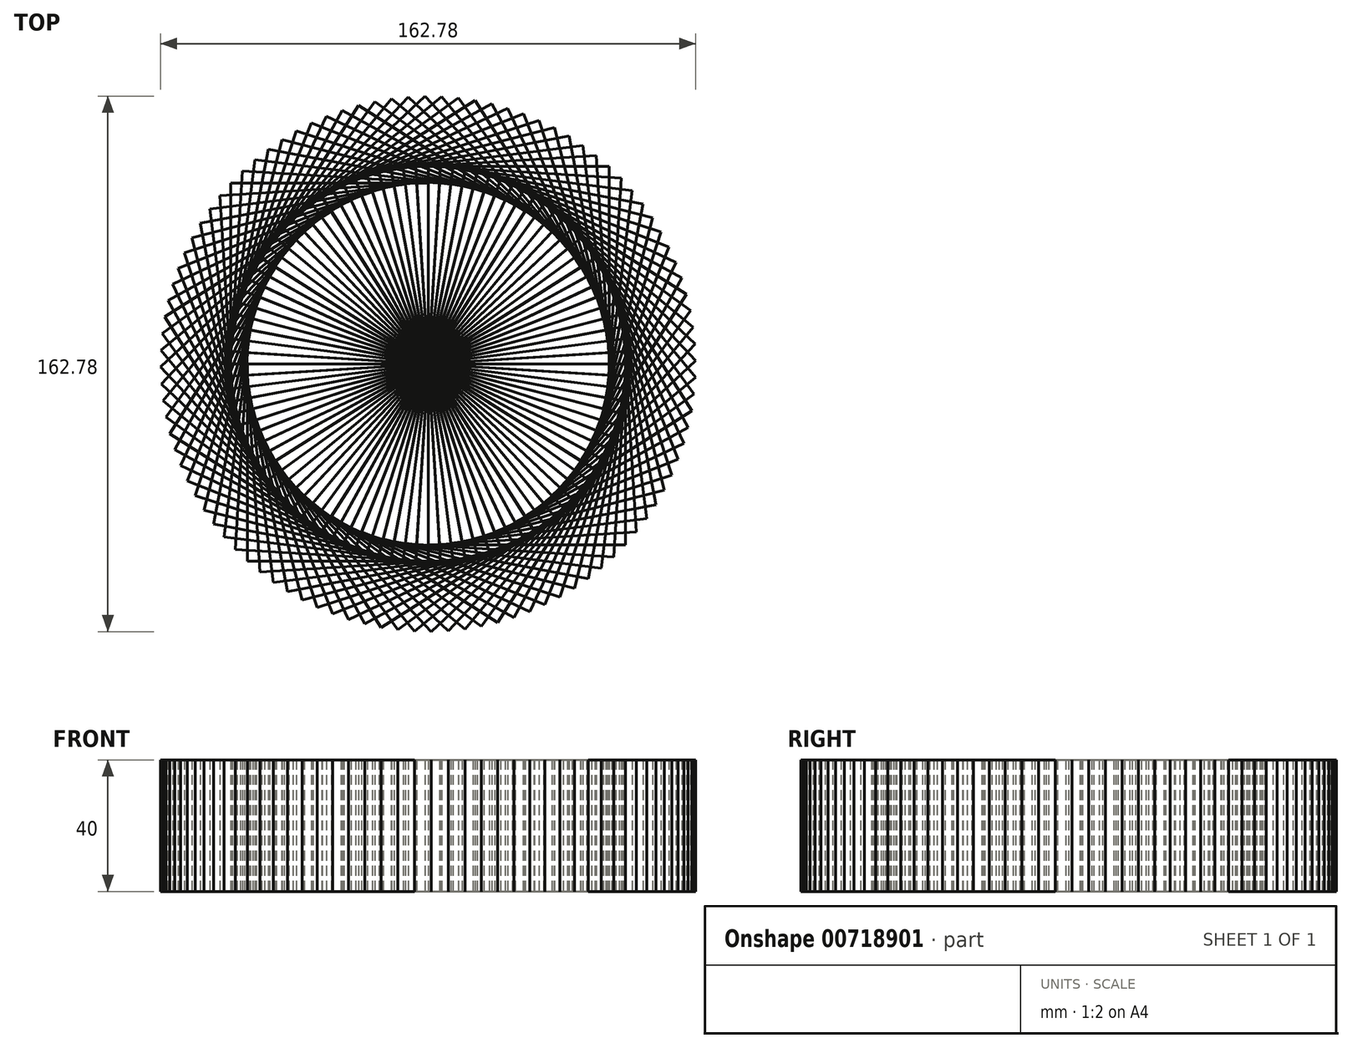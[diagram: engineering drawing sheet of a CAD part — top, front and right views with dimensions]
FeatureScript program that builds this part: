
annotation { "Feature Type Name" : "Feature", "Feature Type Description" : "" }
export const myFeature = defineFeature(function(context is Context, id is Id, definition is map)
    precondition{}
    {
        {
            var Q0;
            Q0=qCreatedBy(makeId("Top.planeOp"),FACE);
            var sketch = newSketch(context, id + "F0", { "sketchPlane" : qUnion([Q0])});
            skLineSegment(sketch, "E0.bottom", {"start": v(0, 0) * mm, "end": v(-60, 0) * mm});
            skLineSegment(sketch, "E0.top", {"start": v(0, 55) * mm, "end": v(-60, 55) * mm});
            skLineSegment(sketch, "E0.left", {"start": v(0, 0) * mm, "end": v(0, 55) * mm});
            skLineSegment(sketch, "E0.right", {"start": v(-60, 0) * mm, "end": v(-60, 55) * mm});
            skSolve(sketch);
        }
        {
            var Q0;
            Q0 = qSketchRegion(id + "F0", true);
            extrude(context, id + "F1", {"entities" : qUnion([Q0]), "depth" : 40 * mm, "offsetDistance" : 25 * mm});
        }
        {
            var Q0;
            Q0=makeQuery(id+"F1.opExtrude","SWEPT_BODY",BODY,{"disambiguationData":[OSD([sQuery(id+"F0.wireOp",EDGE,"E0.bottom"),sQuery(id+"F0.wireOp",EDGE,"E0.top"),sQuery(id+"F0.wireOp",EDGE,"E0.left"),sQuery(id+"F0.wireOp",EDGE,"E0.right")])]});
            var Q1;
            Q1=makeQuery(id+"F1.opExtrude","SWEPT_EDGE",EDGE,{"disambiguationData":[OSD([sQuery(id+"F0.wireOp",EDGE,"E0.bottom"),sQuery(id+"F0.wireOp",EDGE,"E0.left")])]});
            circularPattern(context, id + "F2", {"entities" : qUnion([Q0]), "axis" : qUnion([Q1]), "angle" : 360 * degree, "instanceCount" : 100, "equalSpace" : true});
        }
    });
